# Revit family: Hager-VOLTA-Hollow_wall-IP30-With_Cover-With_DIN-Hosted-ES-es
name_source: partatom
category: Electrical Equipment
units: mm (PartAtom-declared; Revit-internal decimal feet)

## family parameters
Cut with Voids When Loaded = No
Host = Face
Maintain Annotation Orientation = Yes
Panel Configuration = Two Columns, Circuits Across
Part Type = Panelboard
Room Calculation Point = No
Round Connector Dimension = Use Diameter
Shared = No

## types (7) — shared parameters
BC_MODEL_ID = 1547189
BC_OBJECT_ID = 513486
BC_OBJECT_VERSION = #3
Code hager = ADD-EC000214_EU
EF000003 - Método de montaje = Pared hueca
EF000007 - Color = Blanco
EF000008 - Anchura = 348 mm  [stored 1.14173 ft]
EF000024 - Resistente a UV = No
EF000049 - Profundidad = 94 mm  [stored 0.308399 ft]
EF000116 - Número RAL = 9010
EF000118 - Con placa de montaje = No
EF000218 - Profundidad de instalación = 90 mm  [stored 0.295276 ft]
EF000846 - Anchura de montaje = 314 mm  [stored 1.03018 ft]
EF001062 - Versión de CEM = No
EF001088 - Posibilidad de extensión = Yes
EF001134 - Carril DIN = Yes
EF002950 - Ancho en número de espacios modulares = 12
EF004462 - Tipo de cierre = Otros
EF005474 - Grado de protección (IP) = IP30
EF006244 - Tapa/puerta transparente = No
EF006306 - Con candado = No
EF009212 - Versión de la cubierta = Con muesca
EF015777 - Borne neutro = No
EF015941 - Puerta de transmisión de señal = No
ETIM class code = EC000214
ETIM class name = Small distribution board
HG000001 - Número de columnas = 1
HG000002-with door or cover-es = Yes
HG000003-Range-es = VOLTA
HG000005-Thickness-es = 2 mm  [stored 0.00656168 ft]
HG000006-Flush mounted-es = Yes
HG000009-Double swing door-es = No
HG000010-Asymmetric doors-es = No
HG000011-Empty rows from bottom-es = No
HG000012-Door swing angle-es = 90.00°
HG000013-Door on the left-es = No
HG000014-Door on the right-es = Yes
HG000015-Clearance visibility-es = Yes
HG000016-Door 3D visibility-es = Yes
HG000017-Distance between poles-es = 18 mm  [stored 0.0590551 ft]
HG000060-RAL-number = 9010
HG000099-Onfly Template ID-es-ES = 507532
HGEF0002950-Ancho en número de espacios modulares = 12
Manufacturer = Hager
Name = VOLTA-Hollow_wall-IP30-With_Cover-With_DIN-ES
Name BIM&CO = Electricity
Name hager = ADD_Enclosures_EC000214
Uniformat = Low Tension Service & Dist.
Uniformat code = D501001
zero-valued in all types: Default Elevation, EF001131 - Profundidad interna, HG000007-Number of empty columns-es, HG000008-Number of empty rows-es

## per-type parameters (varying)
| type | BC_VARIANT_ID | EF000040 - Altura | EF000266 - Número de filas | EF000332 - Altura de la instalación | EF015776 - Borne de tierra | HG000004-Manufacturer reference-es | HGEF000266-Número de filas |
| VOLTA-Hollow_wall_W348_H356_D94_12_Modular_Spacing-VH12EP | 1174320 | 356 mm  [stored 1.16798 ft] | 1 | 321 mm  [stored 1.05315 ft] | Yes | VH12EP | 1 |
| VOLTA-Hollow_wall_W348_H505_D94_12_Modular_Spacing-VH24EP | 1174321 | 505 mm  [stored 1.65682 ft] | 2 | 471 mm  [stored 1.54528 ft] | Yes | VH24EP | 2 |
| VOLTA-Hollow_wall_W348_H630_D94_12_Modular_Spacing-VH36EP | 1174322 | 630 mm  [stored 2.06693 ft] | 3 | 596 mm  [stored 1.95538 ft] | Yes | VH36EP | 3 |
| VOLTA-Hollow_wall_W348_H630_D94_12_Modular_Spacing-VH36NCT | 1174323 | 630 mm  [stored 2.06693 ft] | 0 | 596 mm  [stored 1.95538 ft] | No | VH36NCT | 0 |
| VOLTA-Hollow_wall_W348_H755_D94_12_Modular_Spacing-VH48EP | 1174324 | 755 mm  [stored 2.47703 ft] | 4 | 721 mm  [stored 2.36549 ft] | Yes | VH48EP | 4 |
| VOLTA-Hollow_wall_W348_H755_D94_12_Modular_Spacing-VH48NCT | 1174325 | 755 mm  [stored 2.47703 ft] | 0 | 721 mm  [stored 2.36549 ft] | No | VH48NCT | 0 |
| VOLTA-Hollow_wall_W348_H880_D94_12_Modular_Spacing-VH60EP | 1174326 | 880 mm  [stored 2.88714 ft] | 5 | 846 mm  [stored 2.77559 ft] | Yes | VH60EP | 5 |

note: column(s) folded — value = type name in every type: Reference

note: [stored X ft] marks values corroborated as IEEE doubles in the binary element streams (Revit-internal decimal feet)

## geometry (parser evidence)
native form markers: Sweep x16
no freeform markers — native parametric forms only
